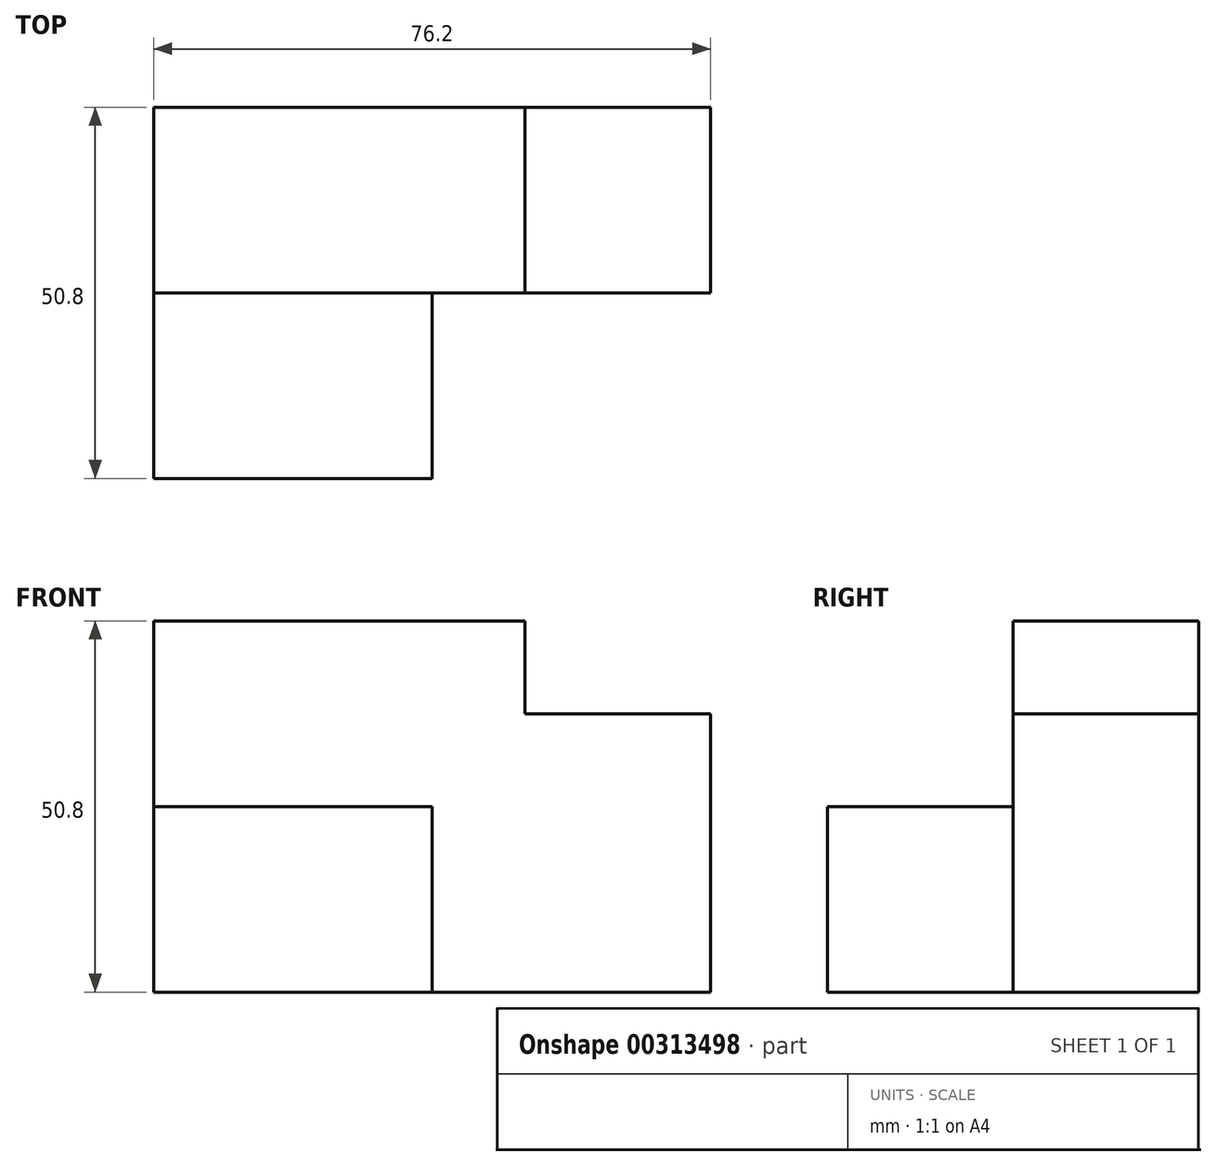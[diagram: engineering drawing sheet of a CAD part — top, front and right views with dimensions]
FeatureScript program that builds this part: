
annotation { "Feature Type Name" : "Feature", "Feature Type Description" : "" }
export const myFeature = defineFeature(function(context is Context, id is Id, definition is map)
    precondition{}
    {
        {
            var Q0;
            Q0=qCreatedBy(makeId("Front.planeOp"),FACE);
            var sketch = newSketch(context, id + "F0", { "sketchPlane" : qUnion([Q0])});
            skLineSegment(sketch, "E0", {"start": v(32.94, -31.05) * mm, "end": v(-43.26, -31.05) * mm});
            skLineSegment(sketch, "E1", {"start": v(-43.26, -31.05) * mm, "end": v(-43.26, 19.75) * mm});
            skLineSegment(sketch, "E2", {"start": v(-43.26, 19.75) * mm, "end": v(7.54, 19.75) * mm});
            skLineSegment(sketch, "E3", {"start": v(7.54, 19.75) * mm, "end": v(7.54, 7.05) * mm});
            skLineSegment(sketch, "E4", {"start": v(32.94, -31.05) * mm, "end": v(32.94, 7.05) * mm});
            skLineSegment(sketch, "E5", {"start": v(32.94, 7.05) * mm, "end": v(7.54, 7.05) * mm});
            skSolve(sketch);
        }
        {
            var Q0;
            Q0 = qSketchRegion(id + "F0", true);
            extrude(context, id + "F1", {"entities" : qUnion([Q0]), "depth" : 25.4 * mm});
        }
        {
            var Q0;
            Q0=makeQuery(id+"F1.opExtrude","CAP_FACE",FACE,{"disambiguationData":[OSD([sQuery(id+"F0.wireOp",EDGE,"E0"),sQuery(id+"F0.wireOp",EDGE,"E1"),sQuery(id+"F0.wireOp",EDGE,"E2"),sQuery(id+"F0.wireOp",EDGE,"E3"),sQuery(id+"F0.wireOp",EDGE,"E4"),sQuery(id+"F0.wireOp",EDGE,"E5")])],"isStart":false});
            var sketch = newSketch(context, id + "F2", { "sketchPlane" : qUnion([Q0])});
            skLineSegment(sketch, "E6", {"start": v(-43.26, -31.05) * mm, "end": v(-43.26, -5.65) * mm});
            skLineSegment(sketch, "E7", {"start": v(-43.26, -5.65) * mm, "end": v(-5.16, -5.65) * mm});
            skLineSegment(sketch, "E8", {"start": v(-5.16, -5.65) * mm, "end": v(-5.16, -31.05) * mm});
            skSolve(sketch);
        }
        {
            var Q0;
            {var subQ0=sQuery(id+"F2.wireOp",EDGE,"E6");Q0=makeQuery(id+"F2.imprint","IMPRINT",FACE,{"disambiguationData":[TD([[makeQuery(id+"F2.imprint","IMPRINT",EDGE,{"derivedFrom":subQ0}),-1.0]])]});}
            extrude(context, id + "F3", {"entities" : qUnion([Q0]), "operationType" : NewBodyOperationType.ADD, "depth" : 25.4 * mm});
        }
    });
